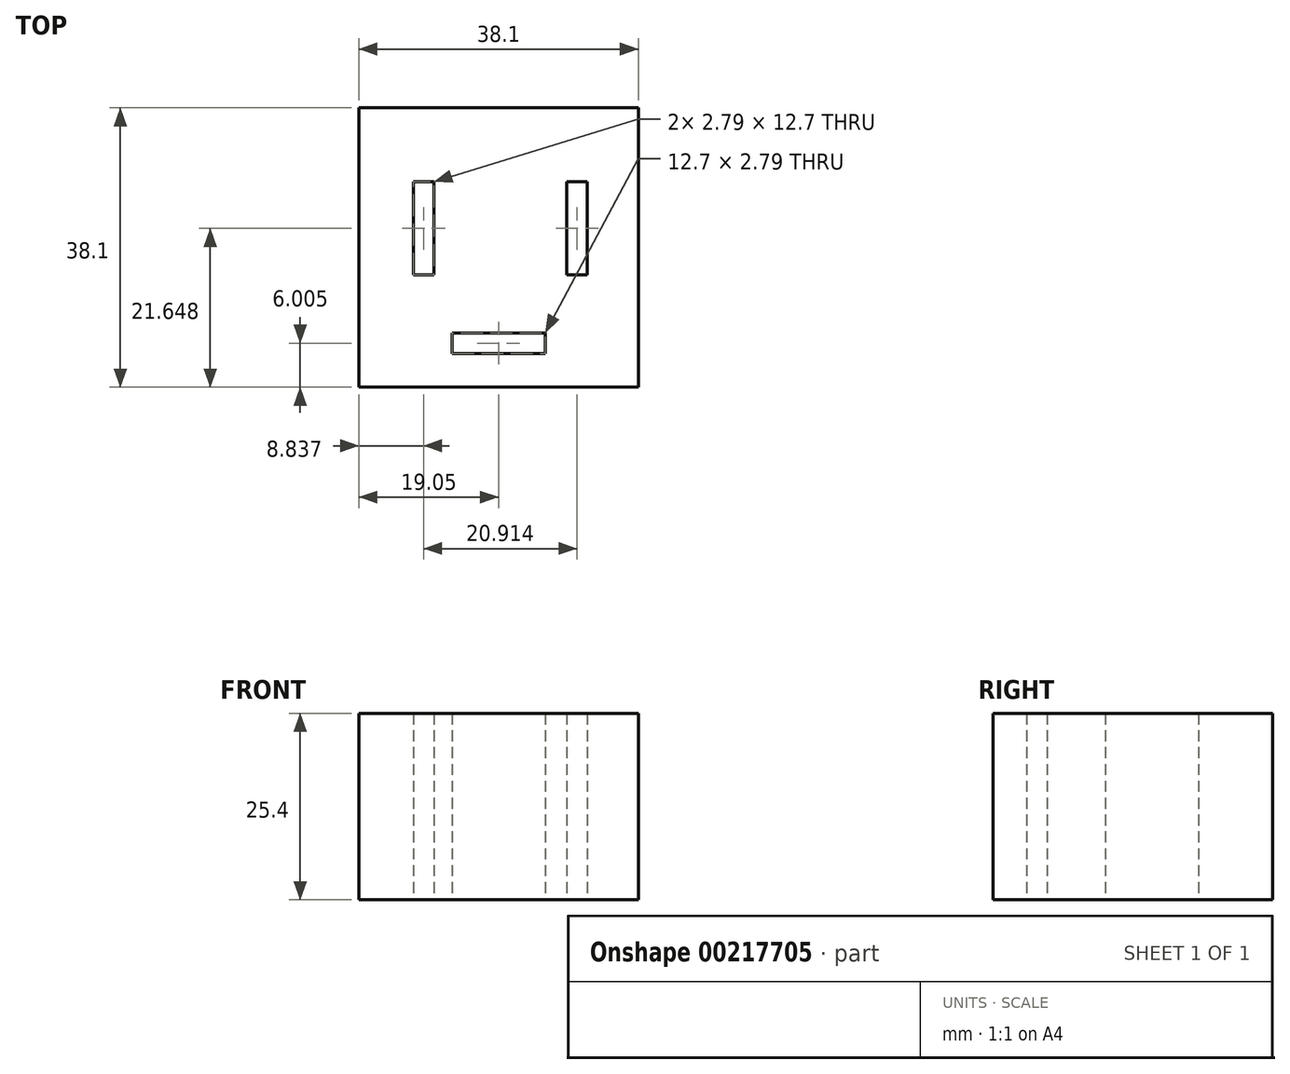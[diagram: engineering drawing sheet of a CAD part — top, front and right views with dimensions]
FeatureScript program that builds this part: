
annotation { "Feature Type Name" : "Feature", "Feature Type Description" : "" }
export const myFeature = defineFeature(function(context is Context, id is Id, definition is map)
    precondition{}
    {
        {
            var Q0;
            Q0=qCreatedBy(makeId("Top.planeOp"),FACE);
            var sketch = newSketch(context, id + "F0", { "sketchPlane" : qUnion([Q0])});
            skLineSegment(sketch, "E0.bottom", {"start": v(-19.05, 19.05) * mm, "end": v(19.05, 19.05) * mm});
            skLineSegment(sketch, "E0.top", {"start": v(-19.05, -19.05) * mm, "end": v(19.05, -19.05) * mm});
            skLineSegment(sketch, "E0.left", {"start": v(-19.05, 19.05) * mm, "end": v(-19.05, -19.05) * mm});
            skLineSegment(sketch, "E0.right", {"start": v(19.05, 19.05) * mm, "end": v(19.05, -19.05) * mm});
            skPoint(sketch, "E0.middle", {"position": v(0, 0) * mm});
            skPoint(sketch, "E1", {"position": v(-6.35, -11.65) * mm});
            skPoint(sketch, "E2", {"position": v(6.35, -11.65) * mm});
            skPoint(sketch, "E3", {"position": v(6.35, -14.44) * mm});
            skLineSegment(sketch, "E4.bottom", {"start": v(-6.35, -11.65) * mm, "end": v(6.35, -11.65) * mm});
            skLineSegment(sketch, "E4.top", {"start": v(-6.35, -14.44) * mm, "end": v(6.35, -14.44) * mm});
            skLineSegment(sketch, "E4.left", {"start": v(-6.35, -11.65) * mm, "end": v(-6.35, -14.44) * mm});
            skLineSegment(sketch, "E4.right", {"start": v(6.35, -11.65) * mm, "end": v(6.35, -14.44) * mm});
            skPoint(sketch, "E5", {"position": v(0, -14.44) * mm});
            skPoint(sketch, "E6", {"position": v(9.3, 8.95) * mm});
            skPoint(sketch, "E7", {"position": v(12.1, 8.95) * mm});
            skPoint(sketch, "E8", {"position": v(9.3, -3.75) * mm});
            skPoint(sketch, "E9", {"position": v(12.1, -3.75) * mm});
            skLineSegment(sketch, "E10", {"start": v(9.3, 8.95) * mm, "end": v(12.1, 8.95) * mm});
            skLineSegment(sketch, "E11", {"start": v(12.1, -3.75) * mm, "end": v(12.1, 8.95) * mm});
            skLineSegment(sketch, "E12", {"start": v(9.3, 8.95) * mm, "end": v(9.3, -3.75) * mm});
            skLineSegment(sketch, "E13", {"start": v(9.3, -3.75) * mm, "end": v(12.1, -3.75) * mm});
            skLineSegment(sketch, "E14", {"start": v(-11.6, 8.95) * mm, "end": v(-8.82, 8.95) * mm});
            skLineSegment(sketch, "E15", {"start": v(-8.82, -3.75) * mm, "end": v(-8.82, 8.95) * mm});
            skLineSegment(sketch, "E16", {"start": v(-11.6, 8.95) * mm, "end": v(-11.6, -3.75) * mm});
            skLineSegment(sketch, "E17", {"start": v(-11.6, -3.75) * mm, "end": v(-8.82, -3.75) * mm});
            skSolve(sketch);
        }
        {
            var Q0;
            Q0=makeQuery(id+"F0.imprint","IMPRINT",FACE,{"disambiguationData":[TD([[makeQuery(id+"F0.imprint","IMPRINT",EDGE,{"derivedFrom":sQuery(id+"F0.wireOp",EDGE,"E0.bottom")}),-1.0]])]});
            extrude(context, id + "F1", {"entities" : qUnion([Q0]), "depth" : 25.4 * mm});
        }
        {
            var Q0;
            Q0 = qSketchRegion(id + "F0", true);
            extrude(context, id + "F2", {"entities" : qUnion([Q0]), "operationType" : NewBodyOperationType.REMOVE, "oppositeDirection" : true, "depth" : 25.4 * mm});
        }
    });
